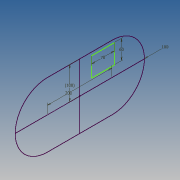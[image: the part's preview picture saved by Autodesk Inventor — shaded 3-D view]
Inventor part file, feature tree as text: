
AUTODESK INVENTOR PART (.ipt)
format: ipt  version: 2014 (Build 180170000, 170)  size: 69,120 bytes
history: native  units: mm
features: sketch x1
ambient origin geometry x8: Origin, YZ Plane, XZ Plane, XY Plane, X Axis, Y Axis, Z Axis, Center Point
feature tree (1):
  sketch  "Sketch1"  dims[d0=200.0mm d1=100.0mm d2=60.0mm d3=70.0mm d4=100.0mm]
